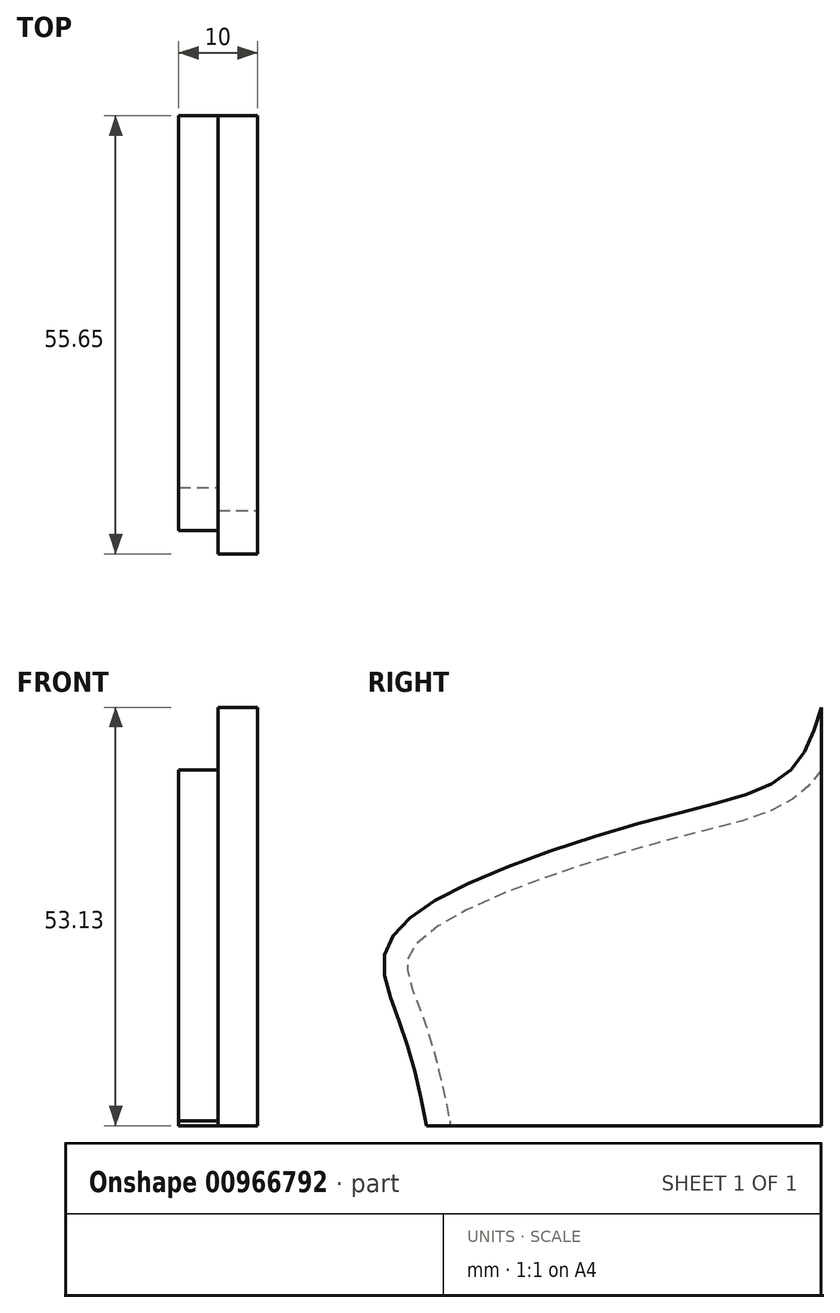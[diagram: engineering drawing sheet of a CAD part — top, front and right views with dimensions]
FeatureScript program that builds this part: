
annotation { "Feature Type Name" : "Feature", "Feature Type Description" : "" }
export const myFeature = defineFeature(function(context is Context, id is Id, definition is map)
    precondition{}
    {
        {
            var Q0;
            Q0=qCreatedBy(makeId("Right.planeOp"),FACE);
            var sketch = newSketch(context, id + "F0", { "sketchPlane" : qUnion([Q0])});
            skFitSpline(sketch, "E0", {"points": [v(39.06, 53.13) * mm, v(34.96, 44.94) * mm, v(19.95, 39.48) * mm, v(-10.08, 28.56) * mm, v(-16.56, 21.06) * mm, v(-14.17, 12.19) * mm, v(-11.1, 0) * mm], "startDerivative": vector(-20.75, -68.08) * mm, "endDerivative": vector(16.35, -79.43) * mm});
            skLineSegment(sketch, "E1", {"start": v(-11.1, 0) * mm, "end": v(39.06, 0) * mm});
            skLineSegment(sketch, "E2", {"start": v(39.06, 0) * mm, "end": v(39.06, 53.13) * mm});
            skSolve(sketch);
        }
        {
            var Q0;
            Q0=makeQuery(id+"F0.imprint","IMPRINT",FACE,{"disambiguationData":[TD([[makeQuery(id+"F0.imprint","IMPRINT",EDGE,{"derivedFrom":sQuery(id+"F0.wireOp",EDGE,"E0")}),1.0]])]});
            extrude(context, id + "F1", {"entities" : qUnion([Q0]), "oppositeDirection" : true, "depth" : 5 * mm, "offsetDistance" : 25 * mm});
        }
        {
            var Q0;
            Q0=makeQuery(id+"F1.opExtrude","CAP_FACE",FACE,{"disambiguationData":[OSD([sQuery(id+"F0.wireOp",EDGE,"E0"),sQuery(id+"F0.wireOp",EDGE,"E1"),sQuery(id+"F0.wireOp",EDGE,"E2")])],"isStart":false});
            var sketch = newSketch(context, id + "F2", { "sketchPlane" : qUnion([Q0])});
            skFitSpline(sketch, "E3.0", {"points": [v(-41.93, 52.26) * mm, v(-41.71, 51.55) * mm, v(-41.27, 50.08) * mm, v(-40.44, 47.8) * mm, v(-39.51, 45.9) * mm, v(-38.54, 44.42) * mm, v(-37.81, 43.54) * mm, v(-37.16, 42.88) * mm, v(-36.45, 42.24) * mm, v(-35.51, 41.54) * mm, v(-34.31, 40.81) * mm, v(-32.63, 39.98) * mm, v(-30.38, 39.14) * mm, v(-27.46, 38.28) * mm, v(-24.81, 37.61) * mm, v(-22.57, 37.05) * mm, v(-20.83, 36.61) * mm, v(-19.02, 36.14) * mm, v(-16.5, 35.45) * mm, v(-13.25, 34.52) * mm, v(-9.24, 33.28) * mm, v(-3.9, 31.5) * mm, v(1.19, 29.58) * mm, v(5.57, 27.6) * mm, v(8.4, 26.12) * mm, v(10.6, 24.7) * mm, v(12.16, 23.38) * mm, v(12.94, 22.41) * mm, v(13.3, 21.75) * mm, v(13.48, 21.29) * mm, v(13.56, 20.93) * mm, v(13.59, 20.63) * mm, v(13.6, 20.29) * mm, v(13.56, 19.8) * mm, v(13.38, 18.85) * mm, v(13.03, 17.7) * mm, v(12.55, 16.4) * mm, v(12.15, 15.34) * mm, v(11.79, 14.41) * mm, v(11.5, 13.63) * mm, v(11.21, 12.83) * mm, v(10.88, 11.82) * mm, v(10.5, 10.59) * mm, v(10.15, 9.35) * mm, v(9.71, 7.7) * mm, v(9.22, 5.6) * mm, v(8.67, 3.1) * mm, v(8.33, 1.43) * mm, v(8.16, 0.6) * mm]});
            skLineSegment(sketch, "E4", {"start": v(-39.06, 0) * mm, "end": v(-39.06, 45.23) * mm});
            skLineSegment(sketch, "E5.0", {"start": v(8.16, 0) * mm, "end": v(-39.06, 0) * mm});
            skLineSegment(sketch, "E6", {"start": v(8.16, 0.6) * mm, "end": v(8.16, 0) * mm});
            skPoint(sketch, "E7.orphan", {"position": v(11.1, 0) * mm});
            skSolve(sketch);
        }
        {
            var Q0;
            Q0 = qSketchRegion(id + "F2", true);
            extrude(context, id + "F3", {"entities" : qUnion([Q0]), "operationType" : NewBodyOperationType.ADD, "depth" : 5 * mm, "offsetDistance" : 25 * mm});
        }
    });
